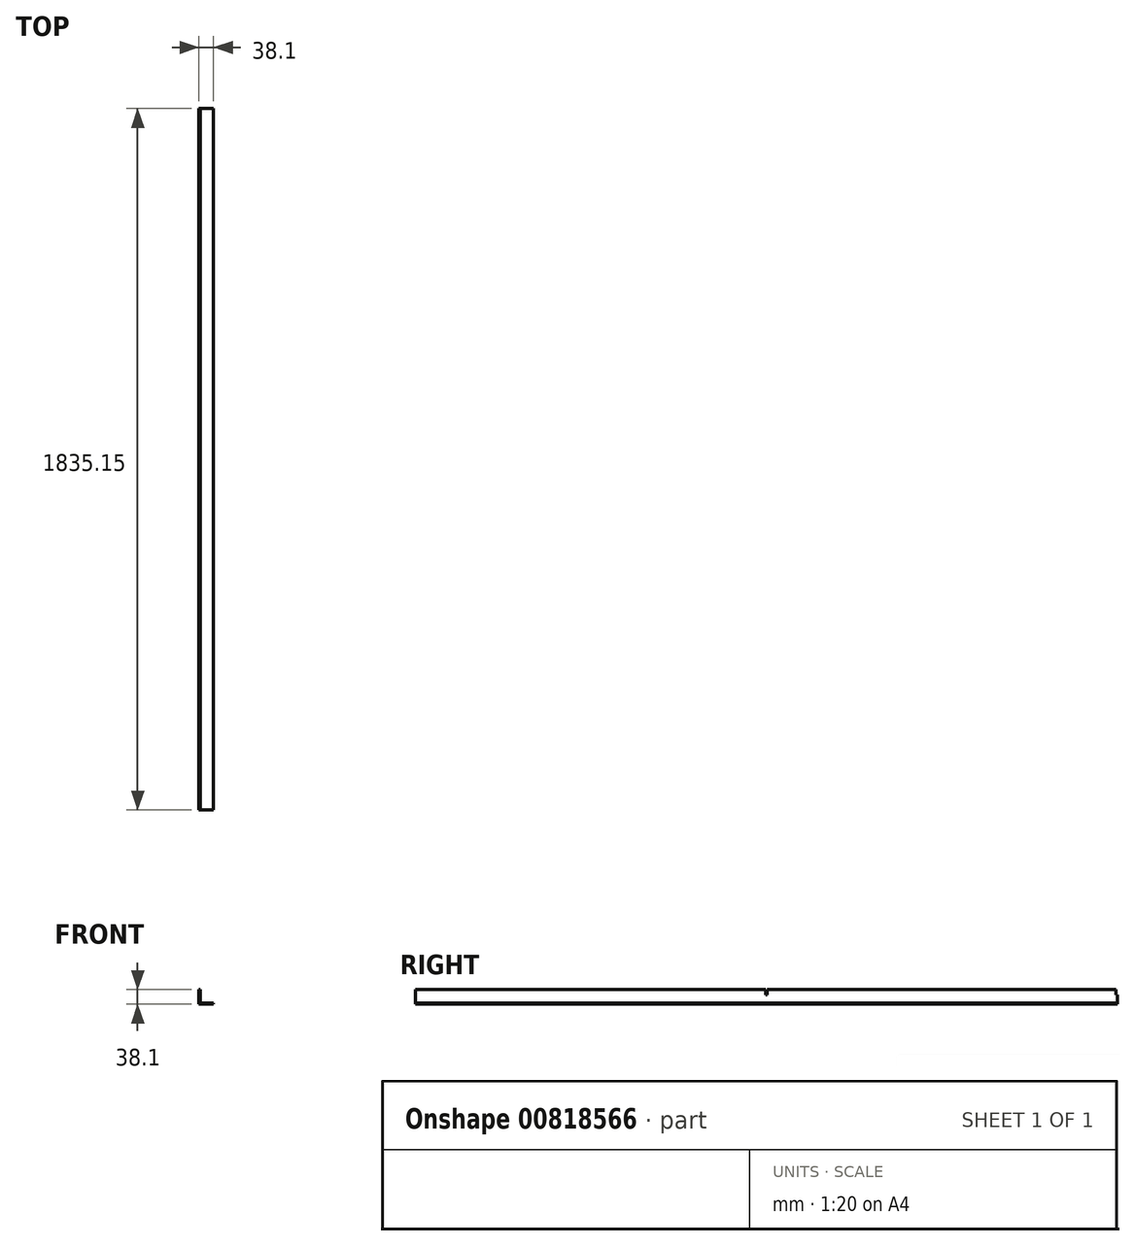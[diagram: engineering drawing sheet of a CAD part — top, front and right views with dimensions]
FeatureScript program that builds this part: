
annotation { "Feature Type Name" : "Feature", "Feature Type Description" : "" }
export const myFeature = defineFeature(function(context is Context, id is Id, definition is map)
    precondition{}
    {
        {
            var Q0;
            Q0=qCreatedBy(makeId("Front.planeOp"),FACE);
            var sketch = newSketch(context, id + "F0", { "sketchPlane" : qUnion([Q0])});
            skLineSegment(sketch, "E0", {"start": v(-21.73, 20.45) * mm, "end": v(-21.73, -17.65) * mm});
            skLineSegment(sketch, "E1", {"start": v(-21.73, -17.65) * mm, "end": v(16.37, -17.65) * mm});
            skLineSegment(sketch, "E2", {"start": v(16.37, -17.65) * mm, "end": v(16.37, -14.47) * mm});
            skLineSegment(sketch, "E3", {"start": v(16.37, -14.47) * mm, "end": v(-18.55, -14.47) * mm});
            skLineSegment(sketch, "E4", {"start": v(-18.55, -14.47) * mm, "end": v(-18.55, 20.45) * mm});
            skLineSegment(sketch, "E5", {"start": v(-18.55, 20.45) * mm, "end": v(-21.73, 20.45) * mm});
            skSolve(sketch);
        }
        {
            var Q0;
            Q0=makeQuery(id+"F0.imprint","IMPRINT",FACE,{"disambiguationData":[TD([[makeQuery(id+"F0.imprint","IMPRINT",EDGE,{"derivedFrom":sQuery(id+"F0.wireOp",EDGE,"E0")}),1.0]])]});
            extrude(context, id + "F1", {"entities" : qUnion([Q0]), "depth" : 1835.15 * mm, "offsetDistance" : 25.4 * mm});
        }
        {
            var Q0;
            Q0=makeQuery(id+"F1.opExtrude","SWEPT_FACE",FACE,{"disambiguationData":[OSD([sQuery(id+"F0.wireOp",EDGE,"E0")])]});
            var sketch = newSketch(context, id + "F2", { "sketchPlane" : qUnion([Q0])});
            skLineSegment(sketch, "E6", {"start": v(919.56, 20.45) * mm, "end": v(919.56, 6.96) * mm});
            skLineSegment(sketch, "E7", {"start": v(919.56, 6.96) * mm, "end": v(915.6, 6.96) * mm});
            skLineSegment(sketch, "E8", {"start": v(915.6, 6.96) * mm, "end": v(915.6, 20.45) * mm});
            skLineSegment(sketch, "E9", {"start": v(915.6, 20.45) * mm, "end": v(919.56, 20.45) * mm});
            skLineSegment(sketch, "E10", {"start": v(1835.15, 6.96) * mm, "end": v(1831.18, 6.96) * mm});
            skLineSegment(sketch, "E11", {"start": v(1831.18, 6.96) * mm, "end": v(1831.18, 20.45) * mm});
            skLineSegment(sketch, "E12", {"start": v(1831.18, 20.45) * mm, "end": v(1835.15, 20.45) * mm});
            skLineSegment(sketch, "E13", {"start": v(1835.15, 20.45) * mm, "end": v(1835.15, 6.96) * mm});
            skLineSegment(sketch, "E14", {"start": v(0, 6.96) * mm, "end": v(3.97, 6.96) * mm});
            skLineSegment(sketch, "E15", {"start": v(3.97, 6.96) * mm, "end": v(3.97, 20.45) * mm});
            skLineSegment(sketch, "E16", {"start": v(3.97, 20.45) * mm, "end": v(0, 20.45) * mm});
            skLineSegment(sketch, "E17", {"start": v(0, 20.45) * mm, "end": v(0, 6.96) * mm});
            skSolve(sketch);
        }
        {
            var Q0;
            Q0=makeQuery(id+"F2.imprint","IMPRINT",FACE,{"disambiguationData":[TD([[makeQuery(id+"F2.imprint","IMPRINT",EDGE,{"derivedFrom":sQuery(id+"F2.wireOp",EDGE,"E6")}),-1.0]])]});
            var Q1;
            Q1=makeQuery(id+"F2.imprint","IMPRINT",FACE,{"disambiguationData":[TD([[makeQuery(id+"F2.imprint","IMPRINT",EDGE,{"derivedFrom":sQuery(id+"F2.wireOp",EDGE,"E14")}),1.0]])]});
            extrude(context, id + "F3", {"entities" : qUnion([Q0, Q1]), "operationType" : NewBodyOperationType.REMOVE, "oppositeDirection" : true, "depth" : 25.4 * mm, "offsetDistance" : 25.4 * mm});
        }
    });
